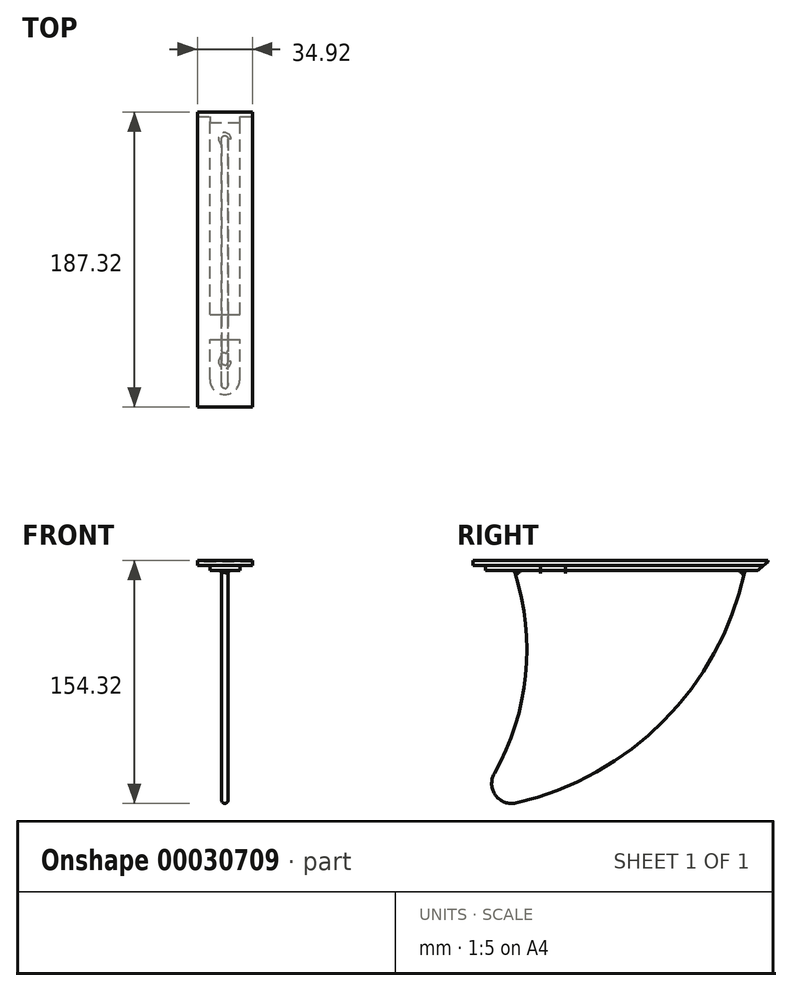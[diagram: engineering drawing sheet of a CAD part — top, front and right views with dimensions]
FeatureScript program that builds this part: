
annotation { "Feature Type Name" : "Feature", "Feature Type Description" : "" }
export const myFeature = defineFeature(function(context is Context, id is Id, definition is map)
    precondition{}
    {
        {
            var Q0;
            Q0=qCreatedBy(makeId("Right.planeOp"),FACE);
            var sketch = newSketch(context, id + "F9", { "sketchPlane" : qUnion([Q0])});
            skLineSegment(sketch, "E0.rect.bottom", {"start": v(0, 0) * mm, "end": v(0, 0) * mm});
            skLineSegment(sketch, "E0.rect.top", {"start": v(0, 0) * mm, "end": v(0, 0) * mm});
            skLineSegment(sketch, "E0.rect.left", {"start": v(0, 0) * mm, "end": v(0, 0) * mm});
            skLineSegment(sketch, "E0.rect.right", {"start": v(0, 0) * mm, "end": v(0, 0) * mm});
            skPoint(sketch, "E0.rect.middle", {"position": v(0, 0) * mm});
            skLineSegment(sketch, "E1.rect.bottom", {"start": v(93.66, 1.59) * mm, "end": v(-93.66, 1.59) * mm});
            skLineSegment(sketch, "E1.rect.top", {"start": v(93.66, -1.59) * mm, "end": v(-93.66, -1.59) * mm});
            skLineSegment(sketch, "E1.rect.left", {"start": v(93.66, 1.59) * mm, "end": v(93.66, -1.59) * mm});
            skLineSegment(sketch, "E1.rect.right", {"start": v(-93.66, 1.59) * mm, "end": v(-93.66, -1.59) * mm});
            skSolve(sketch);
        }
        {
            var Q0;
            Q0 = qSketchRegion(id + "F9", true);
            extrude(context, id + "F0", {"entities" : qUnion([Q0]), "endBound" : BoundingType.SYMMETRIC, "oppositeDirection" : true, "depth" : 34.92 * mm});
        }
        {
            var Q0;
            Q0=makeQuery(id+"F0.opExtrude","SWEPT_FACE",FACE,{"disambiguationData":[OSD([sQuery(id+"F9.wireOp",EDGE,"E1.rect.top")])]});
            var sketch = newSketch(context, id + "F10", { "sketchPlane" : qUnion([Q0])});
            skLineSegment(sketch, "E2.rect.bottom", {"start": v(9.52, 85.72) * mm, "end": v(-9.53, 85.72) * mm});
            skLineSegment(sketch, "E2.rect.top", {"start": v(9.52, -93.66) * mm, "end": v(-9.52, -93.66) * mm});
            skLineSegment(sketch, "E2.rect.left", {"start": v(9.52, 85.72) * mm, "end": v(9.52, -93.66) * mm});
            skLineSegment(sketch, "E2.rect.right", {"start": v(-9.52, 85.72) * mm, "end": v(-9.52, -93.66) * mm});
            skPoint(sketch, "E2.rect.middle", {"position": v(0, -3.97) * mm});
            skSolve(sketch);
        }
        {
            var Q0;
            Q0 = qSketchRegion(id + "F10", true);
            extrude(context, id + "F1", {"entities" : qUnion([Q0]), "operationType" : NewBodyOperationType.ADD, "depth" : 3.17 * mm});
        }
        {
            var Q0;
            Q0=qCreatedBy(makeId("Right.planeOp"),FACE);
            var sketch = newSketch(context, id + "F2", { "sketchPlane" : qUnion([Q0])});
            skArc(sketch, "E3", {"start": v(-80.27, -133.77) * mm, "mid": v(-60.04, -68.1) * mm, "end": v(-69.22, 0) * mm});
            skArc(sketch, "E4.filletArc", {"start": v(-80.27, -133.77) * mm, "mid": v(-79.4, -147.62) * mm, "end": v(-66.36, -152.4) * mm});
            skLineSegment(sketch, "E5", {"start": v(80.01, 0) * mm, "end": v(-69.22, 0) * mm});
            skArc(sketch, "E6", {"start": v(-66.36, -152.4) * mm, "mid": v(29.53, -98) * mm, "end": v(80, 0) * mm});
            skSolve(sketch);
        }
        {
            var Q0;
            Q0 = qSketchRegion(id + "F2", true);
            extrude(context, id + "F3", {"entities" : qUnion([Q0]), "operationType" : NewBodyOperationType.ADD, "endBound" : BoundingType.SYMMETRIC, "depth" : 3.97 * mm});
        }
        {
            var Q0;
            Q0=qCreatedBy(makeId("Right.planeOp"),FACE);
            var sketch = newSketch(context, id + "F4", { "sketchPlane" : qUnion([Q0])});
            skLineSegment(sketch, "E7.bottom", {"start": v(-50.8, -4.76) * mm, "end": v(-34.93, -4.76) * mm});
            skLineSegment(sketch, "E7.top", {"start": v(-50.8, -1.59) * mm, "end": v(-34.93, -1.59) * mm});
            skLineSegment(sketch, "E7.left", {"start": v(-50.8, -4.76) * mm, "end": v(-50.8, -1.59) * mm});
            skLineSegment(sketch, "E7.right", {"start": v(-34.93, -4.76) * mm, "end": v(-34.93, -1.59) * mm});
            skLineSegment(sketch, "E8", {"start": v(-42.86, -1.59) * mm, "end": v(-42.86, -21.49) * mm, "construction": true});
            skSolve(sketch);
        }
        {
            var Q0;
            Q0=makeQuery(id+"F4.imprint","IMPRINT",FACE,{"disambiguationData":[TD([[makeQuery(id+"F4.imprint","IMPRINT",EDGE,{"derivedFrom":sQuery(id+"F4.wireOp",EDGE,"E7.bottom")}),1.0]])]});
            extrude(context, id + "F5", {"entities" : qUnion([Q0]), "operationType" : NewBodyOperationType.REMOVE, "endBound" : BoundingType.THROUGH_ALL, "oppositeDirection" : true, "depth" : 25.4 * mm, "hasSecondDirection" : true, "secondDirectionBound" : SecondDirectionBoundingType.THROUGH_ALL, "secondDirectionOppositeDirection" : false, "secondDirectionDepth" : 25.4 * mm});
        }
        {
            var Q0;
            Q0=makeQuery(id+"F1.opExtrude","SWEPT_EDGE",EDGE,{"disambiguationData":[OSD([sQuery(id+"F10.wireOp",EDGE,"E2.rect.bottom"),sQuery(id+"F10.wireOp",EDGE,"E2.rect.right")])]});
            var Q1;
            Q1=makeQuery(id+"F1.opExtrude","SWEPT_EDGE",EDGE,{"disambiguationData":[OSD([sQuery(id+"F10.wireOp",EDGE,"E2.rect.bottom"),sQuery(id+"F10.wireOp",EDGE,"E2.rect.left")])]});
            fillet(context, id + "F6", {"entities" : qUnion([Q0, Q1]), "radius" : 9.52 * mm, "tangentPropagation" : true, "allowEdgeOverflow" : false});
        }
        {
            var Q0;
            Q0=makeQuery(id+"F1.opExtrude","CAP_EDGE",EDGE,{"disambiguationData":[OSD([sQuery(id+"F10.wireOp",EDGE,"E2.rect.top")])],"isStart":false});
            chamfer(context, id + "F7", {"entities" : qUnion([Q0]), "chamferType" : ChamferType.OFFSET_ANGLE, "width" : 6.6 * mm, "oppositeDirection" : false, "angle" : 40 * degree, "tangentPropagation" : true});
        }
        {
            var Q0;
            Q0=makeQuery(id+"F3.opExtrude","CAP_EDGE",EDGE,{"disambiguationData":[OSD([sQuery(id+"F2.wireOp",EDGE,"E6")])],"isStart":true});
            var Q1;
            Q1=makeQuery(id+"F3.opExtrude","CAP_EDGE",EDGE,{"disambiguationData":[OSD([sQuery(id+"F2.wireOp",EDGE,"E6")])],"isStart":false});
            var Q2;
            {var subQ0=makeQuery(id+"F1.opExtrude","CAP_FACE",FACE,{"disambiguationData":[OSD([sQuery(id+"F10.wireOp",EDGE,"E2.rect.bottom"),sQuery(id+"F10.wireOp",EDGE,"E2.rect.top"),sQuery(id+"F10.wireOp",EDGE,"E2.rect.left"),sQuery(id+"F10.wireOp",EDGE,"E2.rect.right")])],"isStart":false});var subQ1=sQuery(id+"F2.wireOp",EDGE,"E6");var subQ2=makeQuery(id+"F3.opExtrude","CAP_FACE",FACE,{"disambiguationData":[OSD([sQuery(id+"F2.wireOp",EDGE,"E3"),sQuery(id+"F2.wireOp",EDGE,"E4.filletArc"),sQuery(id+"F2.wireOp",EDGE,"E5"),subQ1])],"isStart":false});Q2=makeQuery(id+"F5.boolean.opBoolean","SPLIT",EDGE,{"disambiguationData":[TD([subQ0,subQ2,makeQuery(id+"F3.opExtrude","SWEPT_FACE",FACE,{"disambiguationData":[OSD([subQ1])]}),makeQuery(id+"F5.opExtrude","SWEPT_FACE",FACE,{"disambiguationData":[OSD([sQuery(id+"F4.wireOp",EDGE,"E7.bottom")])]}),makeQuery(id+"F5.opExtrude","SWEPT_FACE",FACE,{"disambiguationData":[OSD([sQuery(id+"F4.wireOp",EDGE,"E7.right")])]})])],"derivedFrom":makeQuery(id+"F3.boolean.opBoolean","INTERSECT",EDGE,{"derivedFrom":[subQ0,subQ2]})});}
            var Q3;
            {var subQ0=makeQuery(id+"F1.opExtrude","CAP_FACE",FACE,{"disambiguationData":[OSD([sQuery(id+"F10.wireOp",EDGE,"E2.rect.bottom"),sQuery(id+"F10.wireOp",EDGE,"E2.rect.top"),sQuery(id+"F10.wireOp",EDGE,"E2.rect.left"),sQuery(id+"F10.wireOp",EDGE,"E2.rect.right")])],"isStart":false});var subQ1=sQuery(id+"F2.wireOp",EDGE,"E3");var subQ2=makeQuery(id+"F3.opExtrude","CAP_FACE",FACE,{"disambiguationData":[OSD([subQ1,sQuery(id+"F2.wireOp",EDGE,"E4.filletArc"),sQuery(id+"F2.wireOp",EDGE,"E5"),sQuery(id+"F2.wireOp",EDGE,"E6")])],"isStart":false});Q3=makeQuery(id+"F5.boolean.opBoolean","SPLIT",EDGE,{"disambiguationData":[TD([subQ0,makeQuery(id+"F3.opExtrude","SWEPT_FACE",FACE,{"disambiguationData":[OSD([subQ1])]}),subQ2,makeQuery(id+"F5.opExtrude","SWEPT_FACE",FACE,{"disambiguationData":[OSD([sQuery(id+"F4.wireOp",EDGE,"E7.bottom")])]}),makeQuery(id+"F5.opExtrude","SWEPT_FACE",FACE,{"disambiguationData":[OSD([sQuery(id+"F4.wireOp",EDGE,"E7.left")])]})])],"derivedFrom":makeQuery(id+"F3.boolean.opBoolean","INTERSECT",EDGE,{"derivedFrom":[subQ0,subQ2]})});}
            fillet(context, id + "F8", {"entities" : qUnion([Q0, Q1, Q2, Q3]), "radius" : 1.98 * mm, "tangentPropagation" : true, "allowEdgeOverflow" : false});
        }
    });
